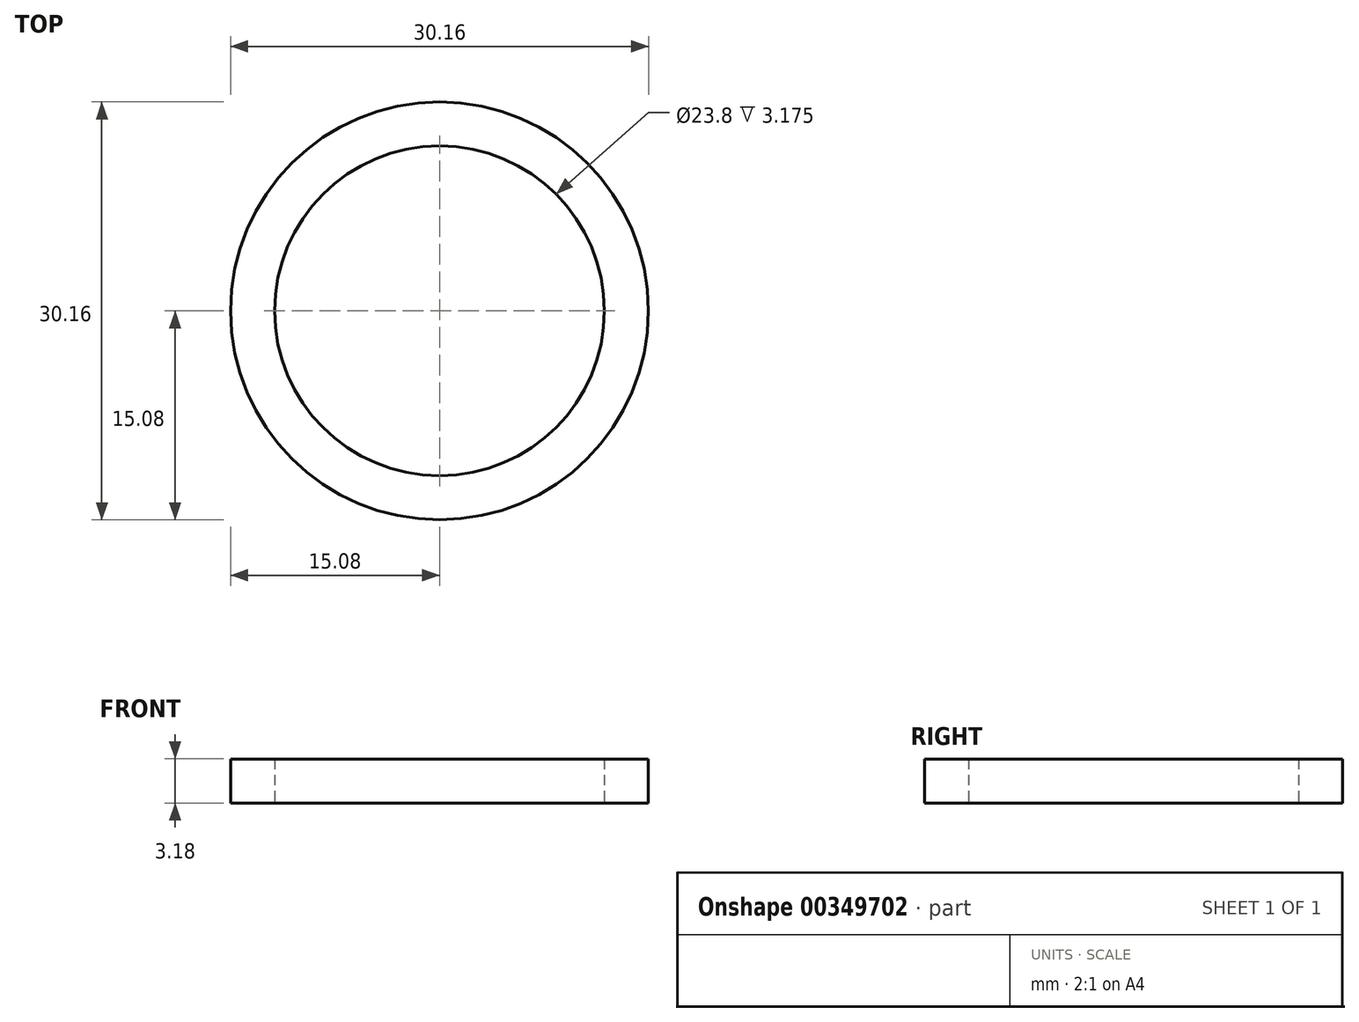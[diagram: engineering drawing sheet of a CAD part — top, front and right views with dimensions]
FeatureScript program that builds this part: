
annotation { "Feature Type Name" : "Feature", "Feature Type Description" : "" }
export const myFeature = defineFeature(function(context is Context, id is Id, definition is map)
    precondition{}
    {
        {
            var Q0;
            Q0=qCreatedBy(makeId("Top.planeOp"),FACE);
            var sketch = newSketch(context, id + "F0", { "sketchPlane" : qUnion([Q0])});
            skCircle(sketch, "E0", {"center": v(0, 0) * mm, "radius": 15.08 * mm});
            skCircle(sketch, "E1", {"center": v(0, 0) * mm, "radius": 11.9 * mm});
            skSolve(sketch);
        }
        {
            var Q0;
            Q0=makeQuery(id+"F0.imprint","IMPRINT",FACE,{"disambiguationData":[TD([[makeQuery(id+"F0.imprint","IMPRINT",EDGE,{"derivedFrom":sQuery(id+"F0.wireOp",EDGE,"E0")}),1.0]])]});
            extrude(context, id + "F1", {"entities" : qUnion([Q0]), "depth" : 3.17 * mm});
        }
    });
